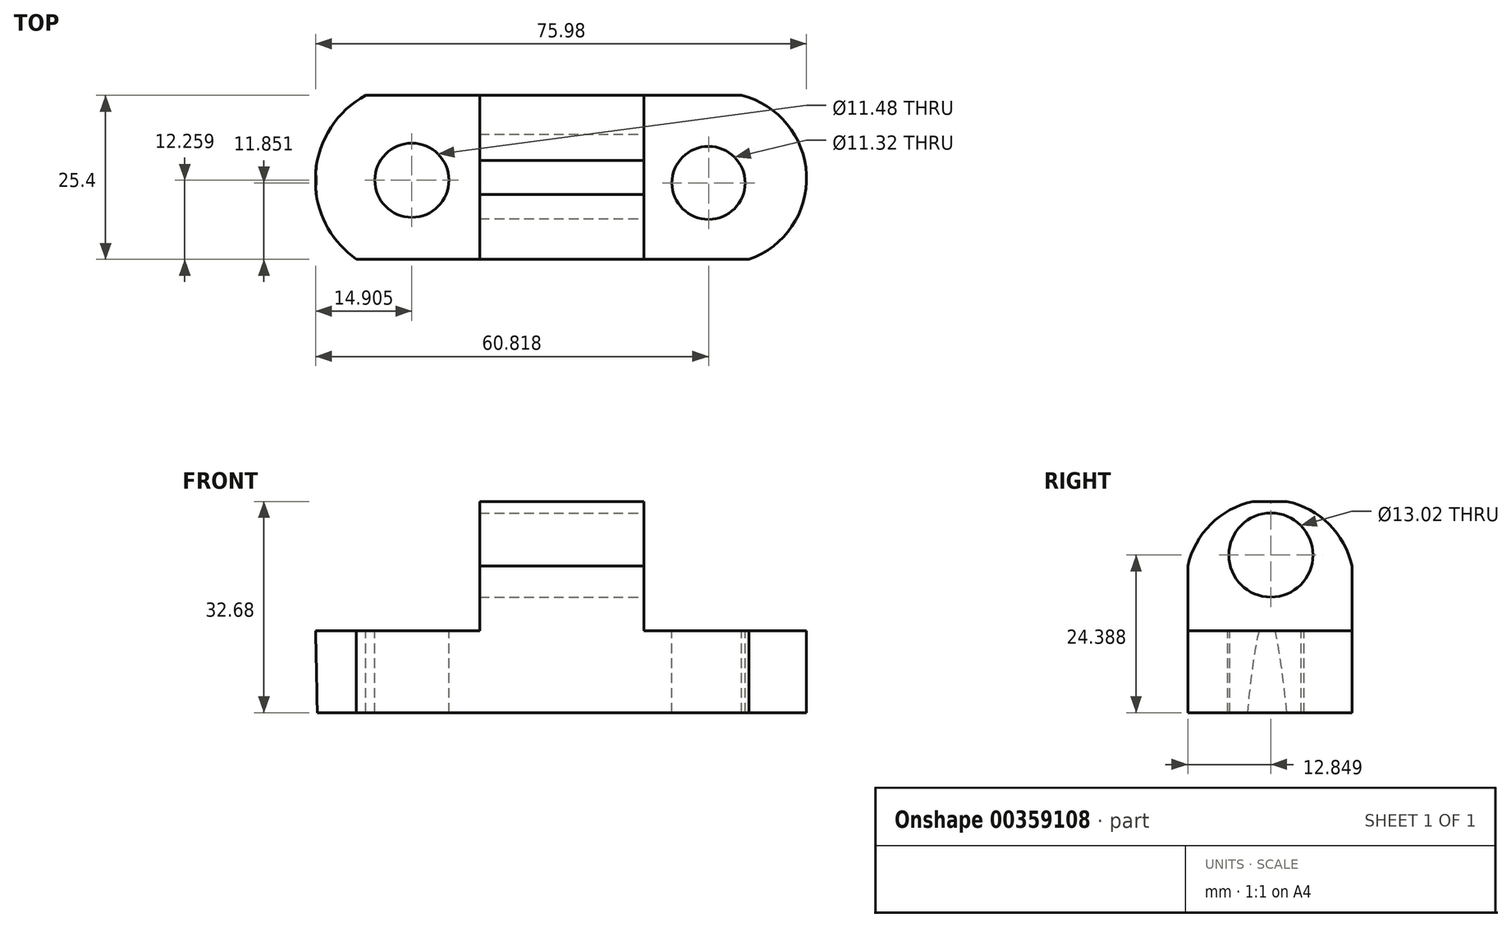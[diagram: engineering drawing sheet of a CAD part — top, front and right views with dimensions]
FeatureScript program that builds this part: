
annotation { "Feature Type Name" : "Feature", "Feature Type Description" : "" }
export const myFeature = defineFeature(function(context is Context, id is Id, definition is map)
    precondition{}
    {
        {
            var Q0;
            Q0=qCreatedBy(makeId("Front.planeOp"),FACE);
            var sketch = newSketch(context, id + "F0", { "sketchPlane" : qUnion([Q0])});
            skLineSegment(sketch, "E0", {"start": v(-57.41, 0) * mm, "end": v(18.52, 0) * mm});
            skLineSegment(sketch, "E1", {"start": v(18.52, 0) * mm, "end": v(18.52, 12.7) * mm});
            skLineSegment(sketch, "E2", {"start": v(18.52, 12.7) * mm, "end": v(-6.88, 12.7) * mm});
            skLineSegment(sketch, "E3", {"start": v(-6.88, 12.7) * mm, "end": v(-6.88, 32.68) * mm});
            skLineSegment(sketch, "E4", {"start": v(-6.88, 32.68) * mm, "end": v(-32.28, 32.68) * mm});
            skLineSegment(sketch, "E5", {"start": v(-32.28, 32.68) * mm, "end": v(-32.28, 12.7) * mm});
            skLineSegment(sketch, "E6", {"start": v(-32.28, 12.7) * mm, "end": v(-57.68, 12.7) * mm});
            skLineSegment(sketch, "E7", {"start": v(-57.68, 12.7) * mm, "end": v(-57.41, 0) * mm});
            skSolve(sketch);
        }
        {
            var Q0;
            Q0 = qSketchRegion(id + "F0", true);
            extrude(context, id + "F1", {"entities" : qUnion([Q0]), "depth" : 25.4 * mm});
        }
        {
            var Q0;
            Q0=makeQuery(id+"F1.opExtrude","SWEPT_FACE",FACE,{"disambiguationData":[OSD([sQuery(id+"F0.wireOp",EDGE,"E3")])]});
            var sketch = newSketch(context, id + "F2", { "sketchPlane" : qUnion([Q0])});
            skArc(sketch, "E8", {"start": v(0, 22.69) * mm, "mid": v(-12.7, 32.95) * mm, "end": v(-25.4, 22.69) * mm});
            skSolve(sketch);
        }
        {
            var Q0;
            {var subQ0=sQuery(id+"F2.wireOp",EDGE,"E8");var subQ1=sQuery(id+"F0.wireOp",EDGE,"E3");var subQ2=makeQuery(id+"F1.opExtrude","CAP_EDGE",EDGE,{"disambiguationData":[OSD([subQ1])],"isStart":false});var subQ3=makeQuery(id+"F2.imprint","INTERSECT",VERTEX,{"derivedFrom":[subQ2,subQ0]});Q0=makeQuery(id+"F2.imprint","IMPRINT",FACE,{"disambiguationData":[TD([[makeQuery(id+"F2.imprint","IMPRINT",EDGE,{"disambiguationData":[TD([[subQ3,1.0]])],"derivedFrom":subQ0}),-1.0]])]});}
            var Q1;
            {var subQ0=sQuery(id+"F2.wireOp",EDGE,"E8");var subQ1=sQuery(id+"F0.wireOp",EDGE,"E3");var subQ2=makeQuery(id+"F1.opExtrude","CAP_EDGE",EDGE,{"disambiguationData":[OSD([subQ1])],"isStart":true});var subQ3=makeQuery(id+"F2.imprint","INTERSECT",VERTEX,{"derivedFrom":[subQ2,subQ0]});Q1=makeQuery(id+"F2.imprint","IMPRINT",FACE,{"disambiguationData":[TD([[makeQuery(id+"F2.imprint","IMPRINT",EDGE,{"disambiguationData":[TD([[subQ3,-1.0]])],"derivedFrom":subQ0}),-1.0]])]});}
            extrude(context, id + "F3", {"entities" : qUnion([Q0, Q1]), "operationType" : NewBodyOperationType.REMOVE, "oppositeDirection" : true, "depth" : 25.4 * mm});
        }
        {
            var Q0;
            Q0=makeQuery(id+"F1.opExtrude","SWEPT_FACE",FACE,{"disambiguationData":[OSD([sQuery(id+"F0.wireOp",EDGE,"E6")])]});
            var sketch = newSketch(context, id + "F4", { "sketchPlane" : qUnion([Q0])});
            skArc(sketch, "E9", {"start": v(-49.92, 0) * mm, "mid": v(-57.7, -12.3) * mm, "end": v(-51.34, -25.4) * mm});
            skArc(sketch, "E10", {"start": v(11.98, -25.4) * mm, "mid": v(18.27, -11.62) * mm, "end": v(8.56, 0) * mm});
            skSolve(sketch);
        }
        {
            var Q0;
            {var subQ0=sQuery(id+"F4.wireOp",EDGE,"E9");var subQ1=sQuery(id+"F0.wireOp",EDGE,"E6");var subQ2=makeQuery(id+"F1.opExtrude","CAP_EDGE",EDGE,{"disambiguationData":[OSD([subQ1])],"isStart":true});var subQ3=makeQuery(id+"F4.imprint","INTERSECT",VERTEX,{"derivedFrom":[subQ2,subQ0]});Q0=makeQuery(id+"F4.imprint","IMPRINT",FACE,{"disambiguationData":[TD([[makeQuery(id+"F4.imprint","IMPRINT",EDGE,{"disambiguationData":[TD([[subQ3,-1.0]])],"derivedFrom":subQ0}),-1.0]])]});}
            var Q1;
            {var subQ0=sQuery(id+"F4.wireOp",EDGE,"E9");var subQ1=sQuery(id+"F0.wireOp",EDGE,"E6");var subQ2=makeQuery(id+"F1.opExtrude","CAP_EDGE",EDGE,{"disambiguationData":[OSD([subQ1])],"isStart":false});var subQ3=makeQuery(id+"F4.imprint","INTERSECT",VERTEX,{"derivedFrom":[subQ2,subQ0]});Q1=makeQuery(id+"F4.imprint","IMPRINT",FACE,{"disambiguationData":[TD([[makeQuery(id+"F4.imprint","IMPRINT",EDGE,{"disambiguationData":[TD([[subQ3,1.0]])],"derivedFrom":subQ0}),-1.0]])]});}
            extrude(context, id + "F5", {"entities" : qUnion([Q0, Q1]), "operationType" : NewBodyOperationType.REMOVE, "oppositeDirection" : true, "depth" : 25.4 * mm});
        }
        {
            var Q0;
            Q0=makeQuery(id+"F1.opExtrude","SWEPT_FACE",FACE,{"disambiguationData":[OSD([sQuery(id+"F0.wireOp",EDGE,"E2")])]});
            var sketch = newSketch(context, id + "F6", { "sketchPlane" : qUnion([Q0])});
            skArc(sketch, "E11", {"start": v(9.41, -25.4) * mm, "mid": v(18.3, -12.28) * mm, "end": v(8.27, 0) * mm});
            skSolve(sketch);
        }
        {
            var Q0;
            {var subQ0=sQuery(id+"F6.wireOp",EDGE,"E11");Q0=makeQuery(id+"F6.imprint","IMPRINT",FACE,{"disambiguationData":[TD([[makeQuery(id+"F6.imprint","IMPRINT",EDGE,{"derivedFrom":subQ0}),-1.0]])]});}
            extrude(context, id + "F7", {"entities" : qUnion([Q0]), "operationType" : NewBodyOperationType.REMOVE, "oppositeDirection" : true, "depth" : 25.4 * mm});
        }
        {
            var Q0;
            Q0=makeQuery(id+"F1.opExtrude","SWEPT_FACE",FACE,{"disambiguationData":[OSD([sQuery(id+"F0.wireOp",EDGE,"E6")])]});
            var sketch = newSketch(context, id + "F8", { "sketchPlane" : qUnion([Q0])});
            skCircle(sketch, "E12", {"center": v(-42.77, -13.14) * mm, "radius": 5.74 * mm});
            skCircle(sketch, "E13", {"center": v(3.14, -13.55) * mm, "radius": 5.66 * mm});
            skSolve(sketch);
        }
        {
            var Q0;
            Q0=makeQuery(id+"F8.imprint","IMPRINT",FACE,{"disambiguationData":[TD([[makeQuery(id+"F8.imprint","IMPRINT",EDGE,{"derivedFrom":sQuery(id+"F8.wireOp",EDGE,"E13")}),1.0]])]});
            var Q1;
            Q1=makeQuery(id+"F8.imprint","IMPRINT",FACE,{"disambiguationData":[TD([[makeQuery(id+"F8.imprint","IMPRINT",EDGE,{"derivedFrom":sQuery(id+"F8.wireOp",EDGE,"E12")}),1.0]])]});
            extrude(context, id + "F9", {"entities" : qUnion([Q0, Q1]), "operationType" : NewBodyOperationType.REMOVE, "oppositeDirection" : true, "depth" : 25.4 * mm});
        }
        {
            var Q0;
            Q0=makeQuery(id+"F1.opExtrude","SWEPT_FACE",FACE,{"disambiguationData":[OSD([sQuery(id+"F0.wireOp",EDGE,"E3")])]});
            var sketch = newSketch(context, id + "F10", { "sketchPlane" : qUnion([Q0])});
            skCircle(sketch, "E14", {"center": v(-12.55, 24.39) * mm, "radius": 6.51 * mm});
            skSolve(sketch);
        }
        {
            var Q0;
            Q0 = qSketchRegion(id + "F10", true);
            extrude(context, id + "F11", {"entities" : qUnion([Q0]), "operationType" : NewBodyOperationType.REMOVE, "oppositeDirection" : true, "depth" : 25.4 * mm});
        }
    });
